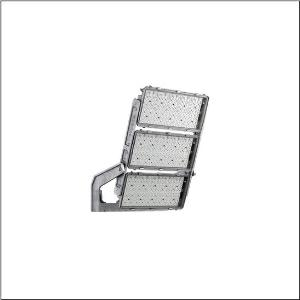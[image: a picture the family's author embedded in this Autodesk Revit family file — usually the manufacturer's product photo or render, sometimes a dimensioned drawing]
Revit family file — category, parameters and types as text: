
# Revit family: floodlight_fl_11_maxi_pro_remote___pl52_5xa779426d01aa_14f9
name_source: partatom
category: Lighting Fixtures
units: mm (PartAtom-declared; Revit-internal decimal feet)

## family parameters
Cut with Voids When Loaded = No
Host = Face
Light Source = No
Part Type = Normal
Room Calculation Point = No
Round Connector Dimension = Use Diameter
Shared = No

## types (1)
- --- (1 x LED, 169140 lm, 1387.6 W, 4000K)
    Apparent Load = 1388 VA
    CIE Flux Codes = 24 55 98 100 100
    Color Rendering = 70
    Color Temperature = 4000K
    Default Elevation = 1800 mm
    Description = Floodlight FL 11  maxi  pro Remote floodlight; light control with lens of PMMA; cover panel of toughened safety glass, transparent; light distribution: PL52, asymmetric direct distribution, LEDcolour temperature: 4000K, rated luminous flux: 169.140lm, colour rendering: CRI > 70, light colour: 740; luminous efficacy: 122lm/W; brightness control: DALI 2 (1 DALI address); with terminal, 8-pole, max. 2.5mm², mains connection: 220..240V/380..400V AC, 50/60Hz, surge voltage resistance: line to ground: 10kV, ECG replaceable separately, LED unit replaceable without ESD environment, dustproof LED module, dimming range 10..100%, no afterglow with DALI off / DMX off command; 1388W floodlight with 3x LED unit of diecast aluminium, coated grey; length: 713mm / width: 651mm / height: 338mm; mounting bracket, of diecast aluminium, uncoated, natural, equipment: Power, protection rating (complete): IP66; insulation class (complete): insulation class I (protective earthing); certification: CE, ENEC, VDE; ball protection: ball impact resistance with accessories, impact resistance: IK07; rated ambient temperature 10°C, only for outdoor installations, permissible operating ambient temperature: -40..+30°C, permissible storage temperature: -40..+85°C; packaging unit: 1 piece

Light Distribution: PL52
    Height = 320 mm
    Lamp = 1 x LED
    Lamp Light Flux = 169140 lm
    Lamp Power = 1387.6 W
    Lamp count = 1
    Length = 1002 mm
    Luminous efficacy = 122 lm/W
    Manufacturer = Siteco
    ModVariant = No
    Model = 5XA779426D01AA
    Mounting Place = Ceiling
    Mounting Type = Surface mounted
    Number of Poles = 1
    OnlyDefault = Yes
    Power Factor = 1
    Product Name = Floodlight FL 11 maxi pro Remote | PL52
    Product group = floodlight | ceiling mounted
    ProductGroupID = 303
    Protection Class = Protection class I
    Protection Degree = IP 66
    RLX_Detail_Level = 1
    RLX_Emergency_Light_Flux = 0 lm
    RLX_Emergency_Type = 0
    RLX_Emergency_Type_DB = No
    RlxData = <blob elided: 52437 chars, md5=0c1655f2>
    Socket = socket
    Standby Power = 0 W
    System Light Flux = 169140 lm
    System Power = 1388 W
    Type Comments = factory setting: luminous flux: 100 % | dim-lin: 254 | 955 mA
    Type Image = l_1006784.jpg
    URL = http://relux.com
    VarID = @adj_046349
    Voltage = 0 V
    Weight = 0.00 kg
    Width = 655 mm

## geometry (parser evidence)
native form markers: Blend x4, Sweep x12
no freeform markers — native parametric forms only
